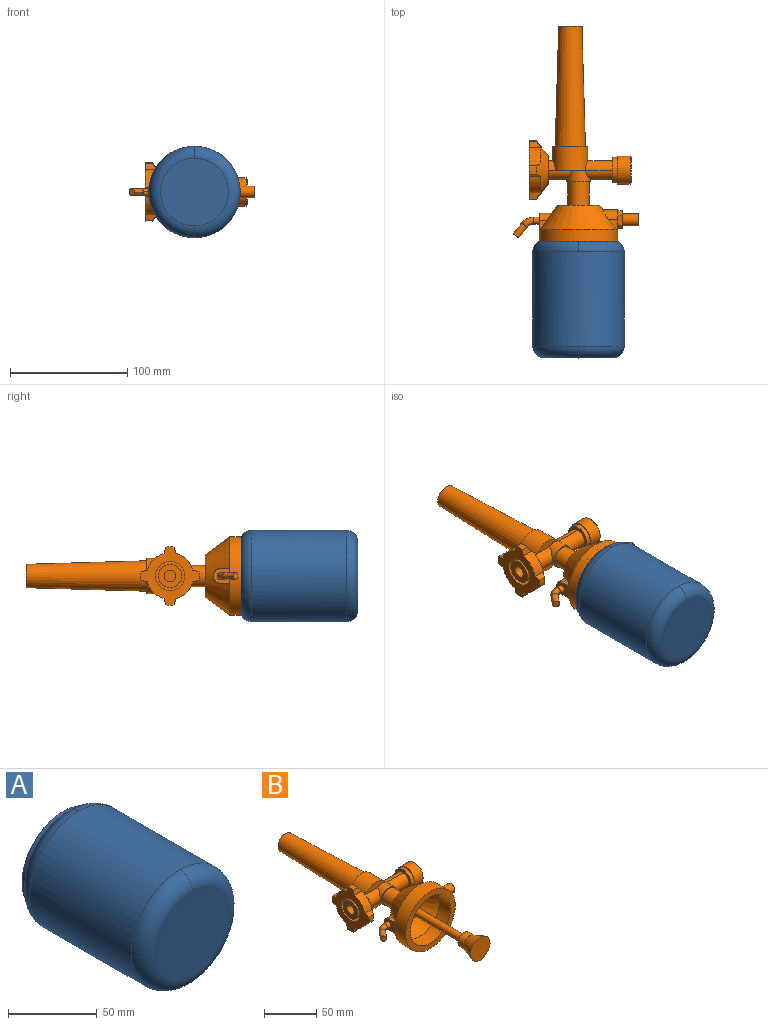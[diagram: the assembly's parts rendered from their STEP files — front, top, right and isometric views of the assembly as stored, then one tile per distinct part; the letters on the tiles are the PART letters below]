
ASSEMBLY  parts=2 mates=1
PART A: 17 faces, bbox 92.5x111.4x92.5 mm
  f0: plane 66.09x66.09mm, normal (0,1,0), area 2642.9mm2, adj f1,f2
  f1: torus R=29mm, axis (0,1,0), area 1542.5mm2, adj f0,f2,f3
  f2: torus R=29mm, axis (0,1,0), area 1542.5mm2, adj f0,f1,f3
  f3: cylinder r=38mm len=80.93mm, axis (0,1,0), area 19323.2mm2, adj f1,f2,f4,f5
  f4: torus R=29mm, axis (0,1,0), area 974.6mm2, adj f3,f5,f6
  f5: torus R=29mm, axis (0,1,0), area 974.6mm2, adj f3,f4,f6
  f6: cone r=0mm half-angle=53.8deg, axis (0,-1,0), area 660.9mm2, adj f4,f5,f7
  f7: cylinder r=31.75mm len=63.51mm, axis (0,1,0), area 641.6mm2, adj f6,f8
  f8: plane 65.51x65.51mm, normal (0,1,0), area 202.6mm2, adj f7,f9
  f9: cylinder r=32.75mm len=65.51mm, axis (0,1,0), area 557.5mm2, adj f8,f10
  f10: cone r=0mm half-angle=53.8deg, axis (0,-1,0), area 569.1mm2, adj f9,f11,f12
  f11: torus R=29mm, axis (0,1,0), area 1108.2mm2, adj f10,f12,f14
  f12: torus R=29mm, axis (0,1,0), area 1108.2mm2, adj f10,f11,f14
  f13: plane 66.09x66.09mm, normal (0,-1,0), area 2642.9mm2, adj f15,f16
  f14: cylinder r=39mm len=80.93mm, axis (0,1,0), area 19831.7mm2, adj f11,f12,f15,f16
  f15: torus R=29mm, axis (0,1,0), area 1745.3mm2, adj f13,f14,f16
  f16: torus R=29mm, axis (0,1,0), area 1745.3mm2, adj f13,f14,f15
PART B: 85 faces, bbox 107.5x256.4x67.2 mm
  f0: plane 10x10mm, normal (-1,0,0), area 78.5mm2, adj f1
  f1: cylinder r=5mm len=10mm, axis (-1,0,0), area 314.2mm2, adj f0,f2
  f2: plane 20x20mm, normal (-1,0,0), area 235.6mm2, adj f1,f3
  f3: cylinder r=10mm len=20mm, axis (-1,0,0), area 628.3mm2, adj f2,f4
  f4: plane 25x25mm, normal (-1,0,0), area 176.7mm2, adj f3,f6
  f5: plane 22x22mm, normal (1,0,0), area 380.1mm2, adj f7
  f6: cylinder r=12.5mm len=25mm, axis (-1,0,0), area 785.4mm2, adj f4,f9
  f7: cone r=0mm half-angle=45deg, axis (-1,0,0), area 102.2mm2, adj f5,f10
  f8: plane 26.5x26.5mm, normal (0,-1,0), area 551.5mm2, adj f12
  f9: plane 50x50mm, normal (-1,0,0), area 941.9mm2, adj f6,f13,f14,f15,f16,f17,f18,f19
  f10: cylinder r=12mm len=24mm, axis (-1,0,0), area 829.4mm2, adj f7,f29
  f11: plane 20x20mm, normal (0,1,0), area 314.2mm2, adj f30
  f12: cone r=0mm half-angle=20.6deg, axis (0,-1,0), area 998.2mm2, adj f8,f31
  f13: plane 9.87x5.4mm, normal (0,-0.96,-0.26), area 44.5mm2, adj f9,f14,f28,f32
  f14: cylinder r=20mm len=14.22mm, axis (-1,0,0), area 208mm2, adj f9,f13,f15,f32
  f15: plane 9.87x5.4mm, normal (0,-0.26,-0.96), area 44.5mm2, adj f9,f14,f16,f32
  f16: cylinder r=25mm len=7.28mm, axis (-1,0,0), area 43.9mm2, adj f9,f15,f17,f32
  f17: plane 9.87x5.4mm, normal (0,-0.26,0.96), area 44.5mm2, adj f9,f16,f18,f32
  f18: cylinder r=20mm len=14.22mm, axis (-1,0,0), area 208mm2, adj f9,f17,f19,f32
  f19: plane 9.87x5.4mm, normal (0,-0.96,0.26), area 44.5mm2, adj f9,f18,f20,f32
  f20: cylinder r=25mm len=7.28mm, axis (-1,0,0), area 43.9mm2, adj f9,f19,f21,f32
  f21: plane 9.87x5.4mm, normal (0,0.96,0.26), area 44.5mm2, adj f9,f20,f22,f32
  f22: cylinder r=20mm len=14.22mm, axis (-1,0,0), area 208mm2, adj f9,f21,f23,f32
  f23: plane 9.87x5.4mm, normal (0,0.26,0.96), area 44.5mm2, adj f9,f22,f24,f32
  f24: cylinder r=25mm len=7.28mm, axis (-1,0,0), area 43.9mm2, adj f9,f23,f25,f32
  f25: plane 9.87x5.4mm, normal (0,0.26,-0.96), area 44.5mm2, adj f9,f24,f26,f32
  f26: cylinder r=20mm len=14.22mm, axis (-1,0,0), area 208mm2, adj f9,f25,f27,f32
  f27: plane 9.87x5.4mm, normal (0,0.96,-0.26), area 44.5mm2, adj f9,f26,f28,f32
  f28: cylinder r=25mm len=7.28mm, axis (-1,0,0), area 43.9mm2, adj f9,f13,f27,f32
  f29: plane 24x24mm, normal (-1,0,0), area 72.3mm2, adj f10,f33
  f30: cone r=0mm half-angle=1.7deg, axis (0,-1,0), area 7445.6mm2, adj f11,f34
  f31: cylinder r=8mm len=16mm, axis (0,1,0), area 402.1mm2, adj f12,f36
  f32: cone r=0mm half-angle=52.2deg, axis (-1,0,0), area 1231.6mm2, adj f13,f14,f15,f16,f17,f18,f19,f20
  f33: cylinder r=11mm len=22mm, axis (-1,0,0), area 276.5mm2, adj f29,f39
  f34: plane 30x30mm, normal (0,1,0), area 175.9mm2, adj f30,f41
  f35: plane 10x10mm, normal (1,0,0), area 78.5mm2, adj f42
  f36: plane 16x16mm, normal (0,1,0), area 150.8mm2, adj f31,f43
  f37: plane 24.18x24.18mm, normal (1,0,0), area 257.9mm2, adj f32,f38,f44
  f38: cylinder r=8mm len=16mm, axis (-1,0,0), area 129mm2, adj f37,f41,f44
  f39: plane 22x22mm, normal (-1,0,0), area 179.1mm2, adj f33,f40,f47
  f40: cylinder r=8mm len=23.31mm, axis (-1,0,0), area 556.2mm2, adj f39,f41,f46,f47,f48
  f41: cylinder r=15mm len=30mm, axis (0,-1,0), area 1675.9mm2, adj f34,f38,f40,f45,f46,f48,f49
  f42: cylinder r=5mm len=14mm, axis (-1,0,0), area 439.8mm2, adj f35,f50
  f43: cylinder r=4mm len=74mm, axis (0,1,0), area 1859.8mm2, adj f36,f51
  f44: cylinder r=8mm len=20mm, axis (-1,0,0), area 449.2mm2, adj f37,f38,f45,f49,f52
  f45: plane 25.12x7mm, normal (0,-1,0), area 109.1mm2, adj f41,f44,f52
  f46: plane 0.57x0.4mm, normal (0,1,0), area 0.1mm2, adj f40,f41,f52
  f47: cylinder r=8mm len=23mm, axis (-1,0,0), area 524.6mm2, adj f39,f40,f52
  f48: plane 0.57x0.4mm, normal (0,1,0), area 0.1mm2, adj f40,f41,f52
  f49: plane 25.12x7mm, normal (0,-1,0), area 109.1mm2, adj f41,f44,f52
  f50: plane 15.63x14.2mm, normal (1,0,0), area 81.2mm2, adj f42,f53,f54,f55,f56,f57,f58
  f51: plane 34.93x34.93mm, normal (0,-1,0), area 907.9mm2, adj f43,f59
  f52: cylinder r=10mm len=20mm, axis (0,1,0), area 405.1mm2, adj f44,f45,f46,f47,f48,f49,f60
  f53: plane 7.1x4mm, normal (0,-0.91,0.42), area 31.4mm2, adj f50,f54,f58,f61
  f54: plane 6.43x4.48mm, normal (0,-0.82,-0.57), area 31.4mm2, adj f50,f53,f55,f61
  f55: plane 7.81x4mm, normal (0,0.08,-1), area 31.4mm2, adj f50,f54,f56,f61
  f56: plane 7.1x4mm, normal (0,0.91,-0.42), area 31.4mm2, adj f50,f55,f57,f61
  f57: plane 6.43x4.48mm, normal (0,0.82,0.57), area 31.4mm2, adj f50,f56,f58,f61
  f58: plane 7.81x4mm, normal (0,-0.08,1), area 31.4mm2, adj f50,f53,f57,f61
  f59: cone r=0mm half-angle=35deg, axis (0,-1,0), area 2357.8mm2, adj f51,f62
  f60: plane 20x20mm, normal (0,-1,0), area 59.7mm2, adj f52,f65
  f61: plane 18x17mm, normal (1,0,0), area 111.7mm2, adj f53,f54,f55,f56,f57,f58,f63,f64
  f62: cylinder r=27.12mm len=54.24mm, axis (0,1,0), area 2556.1mm2, adj f59,f69
  f63: plane 9x1.23mm, normal (0,-1,0), area 3.7mm2, adj f61,f68,f71
  f64: plane 9x1.23mm, normal (0,-1,0), area 3.7mm2, adj f61,f66,f71
  f65: cylinder r=9mm len=20mm, axis (0,1,0), area 1131mm2, adj f60,f70
  f66: plane 8.71x8.02mm, normal (0,0,-1), area 38.3mm2, adj f61,f64,f67,f72
  f67: cylinder r=9.01mm len=18mm, axis (1,0,0), area 303mm2, adj f61,f66,f68,f72
  f68: plane 8.71x8.02mm, normal (0,0,1), area 38.3mm2, adj f61,f63,f67,f72
  f69: plane 67x67mm, normal (0,-1,0), area 1214.8mm2, adj f62,f71
  f70: plane 36x36mm, normal (0,1,0), area 763.4mm2, adj f65,f72
  f71: cylinder r=33.5mm len=67mm, axis (0,1,0), area 3157.3mm2, adj f63,f64,f69,f72,f74,f75
  f72: cone r=0mm half-angle=36.4deg, axis (0,-1,0), area 3678.9mm2, adj f66,f67,f68,f70,f71,f73,f76,f77
  f73: plane 7.92x6.59mm, normal (0,0,1), area 27.5mm2, adj f72,f74,f77,f80
  f74: plane 6.25x0.59mm, normal (0,-1,0), area 1.2mm2, adj f71,f73,f80
  f75: plane 6.25x0.59mm, normal (0,-1,0), area 1.2mm2, adj f71,f76,f80
  f76: plane 7.92x6.59mm, normal (0,0,-1), area 27.5mm2, adj f72,f75,f77,f80
  f77: cylinder r=6.25mm len=12.5mm, axis (-1,0,0), area 178.2mm2, adj f72,f73,f76,f80
  f78: plane 6x4.68mm, normal (-0.63,-0.78,0), area 28.3mm2, adj f79,f81
  f79: cylinder r=3mm len=12.91mm, axis (-0.63,-0.78,0), area 110.7mm2, adj f78,f81,f82
  f80: plane 14.05x12.5mm, normal (-1,0,0), area 130.6mm2, adj f73,f74,f75,f76,f77,f83
  f81: cylinder r=3mm len=12.91mm, axis (-0.63,-0.78,0), area 110.7mm2, adj f78,f79,f84
  f82: torus R=10mm, axis (0,0,1), area 84.3mm2, adj f79,f83,f84
  f83: cylinder r=3mm len=6mm, axis (1,0,0), area 89.9mm2, adj f80,f82,f84
  f84: torus R=10mm, axis (0,0,1), area 84.3mm2, adj f81,f82,f83
PLACE A t=(58.33,-161.64,-31.1)mm fixed
PLACE B t=(16.33,-1.21,-31.1)mm
MATE cylindrical A.f3 <-> B.f12  axis (0,1,0) through (58.33,-59.71,-31.1)mm
